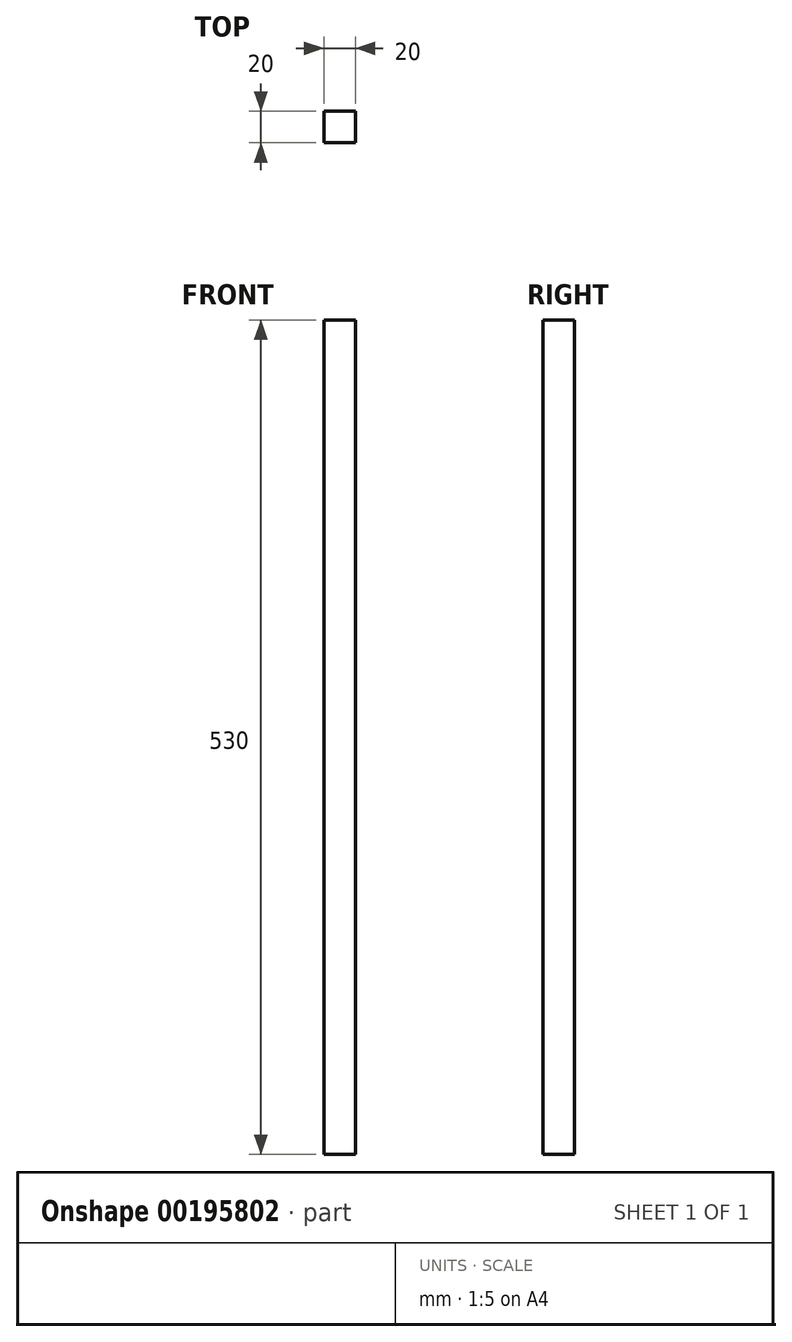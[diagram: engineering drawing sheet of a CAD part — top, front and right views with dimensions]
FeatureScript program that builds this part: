
annotation { "Feature Type Name" : "Feature", "Feature Type Description" : "" }
export const myFeature = defineFeature(function(context is Context, id is Id, definition is map)
    precondition{}
    {
        {
            var Q0;
            Q0=qCreatedBy(makeId("Top.planeOp"),FACE);
            var sketch = newSketch(context, id + "F0", { "sketchPlane" : qUnion([Q0])});
            skLineSegment(sketch, "E0.bottom", {"start": v(-70.8, -20) * mm, "end": v(-50.8, -20) * mm});
            skLineSegment(sketch, "E0.top", {"start": v(-70.8, 0) * mm, "end": v(-50.8, 0) * mm});
            skLineSegment(sketch, "E0.left", {"start": v(-70.8, -20) * mm, "end": v(-70.8, 0) * mm});
            skLineSegment(sketch, "E0.right", {"start": v(-50.8, -20) * mm, "end": v(-50.8, 0) * mm});
            skSolve(sketch);
        }
        {
            var Q0;
            Q0=makeQuery(id+"F0.imprint","IMPRINT",FACE,{"disambiguationData":[TD([[makeQuery(id+"F0.imprint","IMPRINT",EDGE,{"derivedFrom":sQuery(id+"F0.wireOp",EDGE,"E0.bottom")}),1.0]])]});
            extrude(context, id + "F1", {"entities" : qUnion([Q0]), "depth" : 530 * mm});
        }
    });
